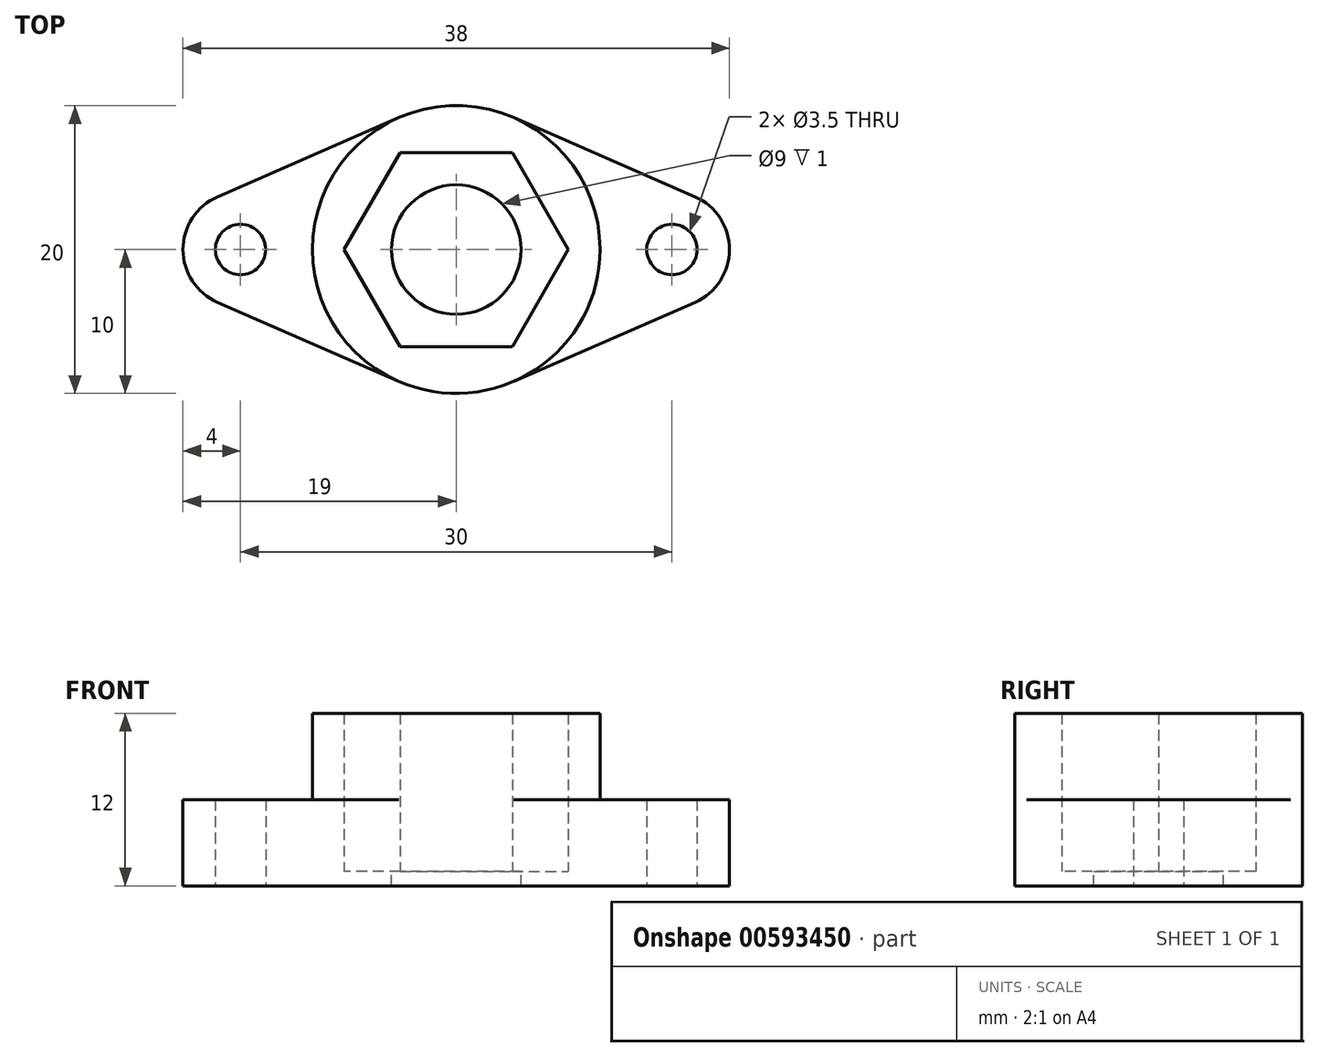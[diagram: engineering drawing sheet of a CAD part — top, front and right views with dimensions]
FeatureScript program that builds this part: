
annotation { "Feature Type Name" : "Feature", "Feature Type Description" : "" }
export const myFeature = defineFeature(function(context is Context, id is Id, definition is map)
    precondition{}
    {
        {
            var Q0;
            Q0=qCreatedBy(makeId("Top.planeOp"),FACE);
            var sketch = newSketch(context, id + "F0", { "sketchPlane" : qUnion([Q0])});
            skCircle(sketch, "E0", {"center": v(0, 0) * mm, "radius": 4.5 * mm});
            skCircle(sketch, "E1.cCircle", {"center": v(0, 0) * mm, "radius": 6.75 * mm, "construction": true});
            skLineSegment(sketch, "E1.0", {"start": v(-3.9, 6.75) * mm, "end": v(3.9, 6.75) * mm});
            skLineSegment(sketch, "E1.1", {"start": v(3.9, 6.75) * mm, "end": v(7.8, 0) * mm});
            skLineSegment(sketch, "E1.2", {"start": v(7.8, 0) * mm, "end": v(3.9, -6.75) * mm});
            skLineSegment(sketch, "E1.3", {"start": v(3.9, -6.75) * mm, "end": v(-3.9, -6.75) * mm});
            skLineSegment(sketch, "E1.4", {"start": v(-3.9, -6.75) * mm, "end": v(-7.8, 0) * mm});
            skLineSegment(sketch, "E1.5", {"start": v(-7.8, 0) * mm, "end": v(-3.9, 6.75) * mm});
            skPoint(sketch, "E1.0.midPoint", {"position": v(0, 6.75) * mm});
            skCircle(sketch, "E2", {"center": v(0, 0) * mm, "radius": 10 * mm});
            skCircle(sketch, "E3", {"center": v(-15, 0) * mm, "radius": 1.75 * mm});
            skCircle(sketch, "E4", {"center": v(15, 0) * mm, "radius": 1.75 * mm});
            skCircle(sketch, "E5", {"center": v(-15, 0) * mm, "radius": 4 * mm});
            skCircle(sketch, "E6", {"center": v(15, 0) * mm, "radius": 4 * mm});
            skLineSegment(sketch, "E7", {"start": v(-15, 0) * mm, "end": v(-16.6, 3.67) * mm});
            skLineSegment(sketch, "E8", {"start": v(-16.6, 3.67) * mm, "end": v(-4, 9.17) * mm});
            skLineSegment(sketch, "E9", {"start": v(-4, 9.17) * mm, "end": v(0, 0) * mm});
            skLineSegment(sketch, "E10", {"start": v(0, 0) * mm, "end": v(4, 9.17) * mm});
            skLineSegment(sketch, "E11", {"start": v(4, 9.17) * mm, "end": v(16.6, 3.67) * mm});
            skLineSegment(sketch, "E12", {"start": v(16.6, 3.67) * mm, "end": v(15, 0) * mm});
            skLineSegment(sketch, "E13", {"start": v(0, 0) * mm, "end": v(-4, -9.17) * mm});
            skLineSegment(sketch, "E14", {"start": v(-4, -9.17) * mm, "end": v(-16.6, -3.67) * mm});
            skLineSegment(sketch, "E15", {"start": v(-16.6, -3.67) * mm, "end": v(-15, 0) * mm});
            skLineSegment(sketch, "E16", {"start": v(0, 0) * mm, "end": v(4, -9.17) * mm});
            skLineSegment(sketch, "E17", {"start": v(4, -9.17) * mm, "end": v(16.6, -3.67) * mm});
            skLineSegment(sketch, "E18", {"start": v(16.6, -3.67) * mm, "end": v(15, 0) * mm});
            skSolve(sketch);
        }
        {
            var Q0;
            {var subQ1=sQuery(id+"F0.wireOp",EDGE,"E1.4");Q0=makeQuery(id+"F0.imprint","IMPRINT",FACE,{"disambiguationData":[TD([[makeQuery(id+"F0.imprint","IMPRINT",EDGE,{"derivedFrom":subQ1}),1.0]])]});}
            var Q1;
            {var subQ0=sQuery(id+"F0.wireOp",EDGE,"E9");var subQ1=sQuery(id+"F0.wireOp",EDGE,"E1.0");var subQ2=makeQuery(id+"F0.imprint","INTERSECT",VERTEX,{"derivedFrom":[subQ1,subQ0]});Q1=makeQuery(id+"F0.imprint","IMPRINT",FACE,{"disambiguationData":[TD([[makeQuery(id+"F0.imprint","IMPRINT",EDGE,{"disambiguationData":[TD([[subQ2,-1.0]])],"derivedFrom":subQ1}),1.0]])]});}
            var Q2;
            {var subQ4=sQuery(id+"F0.wireOp",EDGE,"E1.1");Q2=makeQuery(id+"F0.imprint","IMPRINT",FACE,{"disambiguationData":[TD([[makeQuery(id+"F0.imprint","IMPRINT",EDGE,{"derivedFrom":subQ4}),1.0]])]});}
            var Q3;
            {var subQ0=sQuery(id+"F0.wireOp",EDGE,"E16");var subQ1=sQuery(id+"F0.wireOp",EDGE,"E1.3");var subQ2=makeQuery(id+"F0.imprint","INTERSECT",VERTEX,{"derivedFrom":[subQ1,subQ0]});Q3=makeQuery(id+"F0.imprint","IMPRINT",FACE,{"disambiguationData":[TD([[makeQuery(id+"F0.imprint","IMPRINT",EDGE,{"disambiguationData":[TD([[subQ2,-1.0]])],"derivedFrom":subQ1}),1.0]])]});}
            extrude(context, id + "F1", {"entities" : qUnion([Q0, Q1, Q2, Q3]), "depth" : 11 * mm, "offsetDistance" : 25 * mm});
        }
        {
            var Q0;
            {var subQ0=sQuery(id+"F0.wireOp",EDGE,"E8");Q0=makeQuery(id+"F0.imprint","IMPRINT",FACE,{"disambiguationData":[TD([[makeQuery(id+"F0.imprint","IMPRINT",EDGE,{"derivedFrom":subQ0}),-1.0]])]});}
            var Q1;
            {var subQ0=sQuery(id+"F0.wireOp",EDGE,"E7");var subQ1=sQuery(id+"F0.wireOp",EDGE,"E3");var subQ2=makeQuery(id+"F0.imprint","INTERSECT",VERTEX,{"derivedFrom":[subQ1,subQ0]});Q1=makeQuery(id+"F0.imprint","IMPRINT",FACE,{"disambiguationData":[TD([[makeQuery(id+"F0.imprint","IMPRINT",EDGE,{"disambiguationData":[TD([[subQ2,1.0]])],"derivedFrom":subQ1}),-1.0]])]});}
            var Q2;
            {var subQ0=sQuery(id+"F0.wireOp",EDGE,"E7");var subQ1=sQuery(id+"F0.wireOp",EDGE,"E3");var subQ2=makeQuery(id+"F0.imprint","INTERSECT",VERTEX,{"derivedFrom":[subQ1,subQ0]});Q2=makeQuery(id+"F0.imprint","IMPRINT",FACE,{"disambiguationData":[TD([[makeQuery(id+"F0.imprint","IMPRINT",EDGE,{"disambiguationData":[TD([[subQ2,-1.0]])],"derivedFrom":subQ1}),-1.0]])]});}
            var Q3;
            {var subQ0=sQuery(id+"F0.wireOp",EDGE,"E11");Q3=makeQuery(id+"F0.imprint","IMPRINT",FACE,{"disambiguationData":[TD([[makeQuery(id+"F0.imprint","IMPRINT",EDGE,{"derivedFrom":subQ0}),-1.0]])]});}
            var Q4;
            {var subQ0=sQuery(id+"F0.wireOp",EDGE,"E12");var subQ1=sQuery(id+"F0.wireOp",EDGE,"E4");var subQ2=makeQuery(id+"F0.imprint","INTERSECT",VERTEX,{"derivedFrom":[subQ1,subQ0]});Q4=makeQuery(id+"F0.imprint","IMPRINT",FACE,{"disambiguationData":[TD([[makeQuery(id+"F0.imprint","IMPRINT",EDGE,{"disambiguationData":[TD([[subQ2,-1.0]])],"derivedFrom":subQ1}),-1.0]])]});}
            var Q5;
            {var subQ0=sQuery(id+"F0.wireOp",EDGE,"E12");var subQ1=sQuery(id+"F0.wireOp",EDGE,"E4");var subQ2=makeQuery(id+"F0.imprint","INTERSECT",VERTEX,{"derivedFrom":[subQ1,subQ0]});Q5=makeQuery(id+"F0.imprint","IMPRINT",FACE,{"disambiguationData":[TD([[makeQuery(id+"F0.imprint","IMPRINT",EDGE,{"disambiguationData":[TD([[subQ2,1.0]])],"derivedFrom":subQ1}),-1.0]])]});}
            extrude(context, id + "F2", {"entities" : qUnion([Q0, Q1, Q2, Q3, Q4, Q5]), "operationType" : NewBodyOperationType.ADD, "depth" : 5 * mm, "offsetDistance" : 25 * mm});
        }
        {
            var Q0;
            {var subQ0=sQuery(id+"F0.wireOp",EDGE,"E7");var subQ1=sQuery(id+"F0.wireOp",EDGE,"E3");var subQ2=makeQuery(id+"F0.imprint","INTERSECT",VERTEX,{"derivedFrom":[subQ1,subQ0]});Q0=makeQuery(id+"F0.imprint","IMPRINT",FACE,{"disambiguationData":[TD([[makeQuery(id+"F0.imprint","IMPRINT",EDGE,{"disambiguationData":[TD([[subQ2,-1.0]])],"derivedFrom":subQ1}),-1.0]])]});}
            var Q1;
            {var subQ0=sQuery(id+"F0.wireOp",EDGE,"E7");var subQ1=sQuery(id+"F0.wireOp",EDGE,"E3");var subQ2=makeQuery(id+"F0.imprint","INTERSECT",VERTEX,{"derivedFrom":[subQ1,subQ0]});Q1=makeQuery(id+"F0.imprint","IMPRINT",FACE,{"disambiguationData":[TD([[makeQuery(id+"F0.imprint","IMPRINT",EDGE,{"disambiguationData":[TD([[subQ2,1.0]])],"derivedFrom":subQ1}),-1.0]])]});}
            var Q2;
            {var subQ0=sQuery(id+"F0.wireOp",EDGE,"E8");Q2=makeQuery(id+"F0.imprint","IMPRINT",FACE,{"disambiguationData":[TD([[makeQuery(id+"F0.imprint","IMPRINT",EDGE,{"derivedFrom":subQ0}),-1.0]])]});}
            var Q3;
            {var subQ1=sQuery(id+"F0.wireOp",EDGE,"E1.4");Q3=makeQuery(id+"F0.imprint","IMPRINT",FACE,{"disambiguationData":[TD([[makeQuery(id+"F0.imprint","IMPRINT",EDGE,{"derivedFrom":subQ1}),1.0]])]});}
            var Q4;
            {var subQ0=sQuery(id+"F0.wireOp",EDGE,"E16");var subQ1=sQuery(id+"F0.wireOp",EDGE,"E1.3");var subQ2=makeQuery(id+"F0.imprint","INTERSECT",VERTEX,{"derivedFrom":[subQ1,subQ0]});Q4=makeQuery(id+"F0.imprint","IMPRINT",FACE,{"disambiguationData":[TD([[makeQuery(id+"F0.imprint","IMPRINT",EDGE,{"disambiguationData":[TD([[subQ2,-1.0]])],"derivedFrom":subQ1}),1.0]])]});}
            var Q5;
            {var subQ0=sQuery(id+"F0.wireOp",EDGE,"E9");var subQ1=sQuery(id+"F0.wireOp",EDGE,"E1.0");var subQ2=makeQuery(id+"F0.imprint","INTERSECT",VERTEX,{"derivedFrom":[subQ1,subQ0]});Q5=makeQuery(id+"F0.imprint","IMPRINT",FACE,{"disambiguationData":[TD([[makeQuery(id+"F0.imprint","IMPRINT",EDGE,{"disambiguationData":[TD([[subQ2,-1.0]])],"derivedFrom":subQ1}),1.0]])]});}
            var Q6;
            {var subQ4=sQuery(id+"F0.wireOp",EDGE,"E1.1");Q6=makeQuery(id+"F0.imprint","IMPRINT",FACE,{"disambiguationData":[TD([[makeQuery(id+"F0.imprint","IMPRINT",EDGE,{"derivedFrom":subQ4}),1.0]])]});}
            var Q7;
            {var subQ0=sQuery(id+"F0.wireOp",EDGE,"E11");Q7=makeQuery(id+"F0.imprint","IMPRINT",FACE,{"disambiguationData":[TD([[makeQuery(id+"F0.imprint","IMPRINT",EDGE,{"derivedFrom":subQ0}),-1.0]])]});}
            var Q8;
            {var subQ0=sQuery(id+"F0.wireOp",EDGE,"E12");var subQ1=sQuery(id+"F0.wireOp",EDGE,"E4");var subQ2=makeQuery(id+"F0.imprint","INTERSECT",VERTEX,{"derivedFrom":[subQ1,subQ0]});Q8=makeQuery(id+"F0.imprint","IMPRINT",FACE,{"disambiguationData":[TD([[makeQuery(id+"F0.imprint","IMPRINT",EDGE,{"disambiguationData":[TD([[subQ2,-1.0]])],"derivedFrom":subQ1}),-1.0]])]});}
            var Q9;
            {var subQ0=sQuery(id+"F0.wireOp",EDGE,"E12");var subQ1=sQuery(id+"F0.wireOp",EDGE,"E4");var subQ2=makeQuery(id+"F0.imprint","INTERSECT",VERTEX,{"derivedFrom":[subQ1,subQ0]});Q9=makeQuery(id+"F0.imprint","IMPRINT",FACE,{"disambiguationData":[TD([[makeQuery(id+"F0.imprint","IMPRINT",EDGE,{"disambiguationData":[TD([[subQ2,1.0]])],"derivedFrom":subQ1}),-1.0]])]});}
            var Q10;
            {var subQ0=sQuery(id+"F0.wireOp",EDGE,"E1.4");Q10=makeQuery(id+"F0.imprint","IMPRINT",FACE,{"disambiguationData":[TD([[makeQuery(id+"F0.imprint","IMPRINT",EDGE,{"derivedFrom":subQ0}),-1.0]])]});}
            var Q11;
            {var subQ0=sQuery(id+"F0.wireOp",EDGE,"E13");var subQ1=sQuery(id+"F0.wireOp",EDGE,"E0");var subQ2=makeQuery(id+"F0.imprint","INTERSECT",VERTEX,{"derivedFrom":[subQ1,subQ0]});Q11=makeQuery(id+"F0.imprint","IMPRINT",FACE,{"disambiguationData":[TD([[makeQuery(id+"F0.imprint","IMPRINT",EDGE,{"disambiguationData":[TD([[subQ2,-1.0]])],"derivedFrom":subQ1}),-1.0]])]});}
            var Q12;
            {var subQ0=sQuery(id+"F0.wireOp",EDGE,"E1.1");Q12=makeQuery(id+"F0.imprint","IMPRINT",FACE,{"disambiguationData":[TD([[makeQuery(id+"F0.imprint","IMPRINT",EDGE,{"derivedFrom":subQ0}),-1.0]])]});}
            var Q13;
            {var subQ0=sQuery(id+"F0.wireOp",EDGE,"E9");var subQ1=sQuery(id+"F0.wireOp",EDGE,"E0");var subQ2=makeQuery(id+"F0.imprint","INTERSECT",VERTEX,{"derivedFrom":[subQ1,subQ0]});Q13=makeQuery(id+"F0.imprint","IMPRINT",FACE,{"disambiguationData":[TD([[makeQuery(id+"F0.imprint","IMPRINT",EDGE,{"disambiguationData":[TD([[subQ2,1.0]])],"derivedFrom":subQ1}),-1.0]])]});}
            extrude(context, id + "F3", {"entities" : qUnion([Q0, Q1, Q2, Q3, Q4, Q5, Q6, Q7, Q8, Q9, Q10, Q11, Q12, Q13]), "operationType" : NewBodyOperationType.ADD, "oppositeDirection" : true, "depth" : 1 * mm, "offsetDistance" : 25 * mm});
        }
        {
            var Q0;
            {var subQ0=sQuery(id+"F0.wireOp",EDGE,"E12");var subQ1=sQuery(id+"F0.wireOp",EDGE,"E4");var subQ2=makeQuery(id+"F0.imprint","INTERSECT",VERTEX,{"derivedFrom":[subQ1,subQ0]});Q0=makeQuery(id+"F0.imprint","IMPRINT",FACE,{"disambiguationData":[TD([[makeQuery(id+"F0.imprint","IMPRINT",EDGE,{"disambiguationData":[TD([[subQ2,-1.0]])],"derivedFrom":subQ1}),1.0]])]});}
            var Q1;
            {var subQ0=sQuery(id+"F0.wireOp",EDGE,"E12");var subQ1=sQuery(id+"F0.wireOp",EDGE,"E4");var subQ2=makeQuery(id+"F0.imprint","INTERSECT",VERTEX,{"derivedFrom":[subQ1,subQ0]});Q1=makeQuery(id+"F0.imprint","IMPRINT",FACE,{"disambiguationData":[TD([[makeQuery(id+"F0.imprint","IMPRINT",EDGE,{"disambiguationData":[TD([[subQ2,1.0]])],"derivedFrom":subQ1}),1.0]])]});}
            var Q2;
            {var subQ0=sQuery(id+"F0.wireOp",EDGE,"E7");var subQ1=sQuery(id+"F0.wireOp",EDGE,"E3");var subQ2=makeQuery(id+"F0.imprint","INTERSECT",VERTEX,{"derivedFrom":[subQ1,subQ0]});Q2=makeQuery(id+"F0.imprint","IMPRINT",FACE,{"disambiguationData":[TD([[makeQuery(id+"F0.imprint","IMPRINT",EDGE,{"disambiguationData":[TD([[subQ2,1.0]])],"derivedFrom":subQ1}),1.0]])]});}
            var Q3;
            {var subQ0=sQuery(id+"F0.wireOp",EDGE,"E7");var subQ1=sQuery(id+"F0.wireOp",EDGE,"E3");var subQ2=makeQuery(id+"F0.imprint","INTERSECT",VERTEX,{"derivedFrom":[subQ1,subQ0]});Q3=makeQuery(id+"F0.imprint","IMPRINT",FACE,{"disambiguationData":[TD([[makeQuery(id+"F0.imprint","IMPRINT",EDGE,{"disambiguationData":[TD([[subQ2,-1.0]])],"derivedFrom":subQ1}),1.0]])]});}
            extrude(context, id + "F4", {"entities" : qUnion([Q0, Q1, Q2, Q3]), "operationType" : NewBodyOperationType.ADD, "depth" : 5 * mm, "offsetDistance" : 25 * mm});
        }
        {
            var Q0;
            Q0=sQuery(id+"F0.wireOp",VERTEX,"E12.end");
            var Q1;
            Q1=sQuery(id+"F0.wireOp",VERTEX,"E7.start");
            var Q2;
            Q2=makeQuery(id+"F1.opExtrude","SWEPT_BODY",BODY,{"disambiguationData":[OSD([sQuery(id+"F0.wireOp",EDGE,"E1.0"),sQuery(id+"F0.wireOp",EDGE,"E1.1"),sQuery(id+"F0.wireOp",EDGE,"E1.2"),sQuery(id+"F0.wireOp",EDGE,"E1.3"),sQuery(id+"F0.wireOp",EDGE,"E1.4"),sQuery(id+"F0.wireOp",EDGE,"E1.5"),sQuery(id+"F0.wireOp",EDGE,"E2")])]});
            hole(context, id + "F5", {"style" : HoleStyle.SIMPLE, "endStyle" : HoleEndStyle.THROUGH, "oppositeDirection" : true, "holeDiameter" : 3.5 * mm, "majorDiameter" : 5 * mm, "isTappedThrough" : true, "tappedDepth" : 12 * mm, "tapClearance" : 3, "locations" : qUnion([Q0, Q1]), "scope" : qUnion([Q2])});
        }
    });
